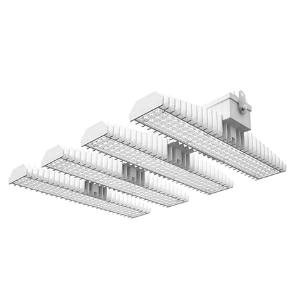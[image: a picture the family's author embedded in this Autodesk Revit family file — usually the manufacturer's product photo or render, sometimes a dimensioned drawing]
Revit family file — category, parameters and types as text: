
# Revit family: 3f_filippi_-_3f_lem_medio_3f_filippi_-_58913_a0811_-_3f_lem_4_led_200_dali_cr_medio___vt_bfc1
name_source: partatom
category: Lighting Fixtures
units: mm (PartAtom-declared; Revit-internal decimal feet)

## family parameters
Cut with Voids When Loaded = No
Host = Face
Light Source = No
Part Type = Normal
Room Calculation Point = No
Round Connector Dimension = Use Diameter
Shared = No

## types (1)
- 3F Filippi - 3F LEM Medio (1 x LED, 30958 lm, 218 W, 4000 K)
    Apparent Load = 218 VA
    Approval mark = CE
    CIE Flux Codes = 83 96 99 100 100
    Color Rendering = 80
    Color Temperature = 4000 K
    Control Gear = Electronic transformer
    Default Elevation = 1800 mm
    Description = Industrial luminaire with high light output and high luminous efficiency designed with the most innovative technologies for environments with temperature up to 55°C.

ILLUMINOTECHNICAL
Luminous efficiency 100% (DLOR 99%, ULOR 1%).
Initial luminous flux of the luminaire 30958 lm.
Medium distribution with rectangular shape.
Installation Interdistance Transv.D = 1.02 x hu - Long.D = 1.06 x hu.
Tabular UGR (CIE 117 - 4H-8H; S=0.25H; 70/50/20): RUG 18.9 - 18.5.
Beam angle: 65° - 67°.
Luminous efficacy 142 lm/W.
Lifetime (L93/B10): 30000 h. (tq+25°C)
Lifetime (L90/B10): 50000 h. (tq+25°C)
Lifetime (L85/B10): 80000 h. (tq+25°C)
Lifetime (L80/B10): 100000 h. (tq+25°C)
Lifetime (L85/B10): 50000 h. (tq+55°C)
Sudden decreased luminous flux after 50000 hours: 0% (C0).
Photobiological safety in compliance with IEC/TR 62778: RG0 risk exempt, (IEC 62471).
In compliance with IEC/EN 62722-2-1 - IEC/EN 62717 standards.

SOURCE
4 Mid-Power linear LED modules 50W/840.
Energy efficiency class (UE 2019/2020 - UE 2019/2015): C.
CIE 13.3 Colour rendering index: CRI >80 (R9 <50%).
IES TM-30 Fidelity Index: Rf = 84 Rg = 95.
CCT nominal colour temperature 4000 K.
Colour initial tolerance (MacAdam): SDCM 3.

MECHANICAL
Passive modular heatsinks in die-casted aluminium, painted in white colour.
To optimize the thermal management of the LED module, the heatsinks are oversized and provided with self-cleaning of cooling fins.
Wiring body in aluminium and galvanised steel anchored solidly to the sinks and thermally separated.
3F Lens lenses with high luminous efficiency, transparent methacrylate (PMMA), fixed to the LED modules.
Fixing brackets in stainless steel.
Luminaire with limited surface temperature. - D - (EN 60598-2-24)
Dimensions: 757x542 mm, height 133 mm. Weight 18.978 kg.
IP65 protection degree.
Mechanical strength to impacts IK06 (1 joule).
Glow-wire test resistance 650°C.

ELECTRICAL
Halogen Free DALI-2 DATI (Parts 251, 252, 253), PUSH-DIM, electronic wiring 230V-50/60Hz, power factor 0.97 at full load, THD <25%, constant output current, class I, 2 driver, 2 DALI addresses.
Power of the luminaire 218 W.
ENEC - CE.
Flicker: <4%.
Luminaire compliant with EN 60598-2-22 for power supply from a centralised emergency system CPSS (Central Power Supply System), not incorporated in the luminaire - high risk areas excluded. The default power and flux are 100% in AC and 15% in DC.
Ambient temperature from -30°C to +55°C.
Temperature class T6 max 85°C.
Quick connection via M25 5P connector with 9-13 mm tightening range.
Power unit positioned on a separate compartment by the LED module to ensure optimum temperatures of cabling components, to be inspectable and maintainable.
Relative humidity UR: <85%.

INSTALLATION
Ceiling / Suspended / Wall.
All accessories dedicated to this product are available on the Catalog and on our website www.3F-Filippi.com.

ACCESSORIES
A0811 - VT transparent glass, tempered, not flammable, with sealing gasket.
One required for each light module. The pack contains 10 pieces.

APPLICATIONS
In commercial environments, exhibition and industrial areas, stores, open areas.
Applications with high ambient temperature up to 55°C.
Environments in which it is necessary a total protection against falling fragments (eg environments with foodstuffs or machines with moving parts or with extreme temperature changes), use luminaires with polycarbonate lenses.

LIGHT MANAGEMENT
Recommended minimum setting: 10%.
The luminaire, equipped with (DALI-2 DATI) driver, can be controlled manually with 3F Easy Dim technology or automatically/manually with wired or wireless DALI/D2D control systems.
The D2D driver guarantees interoperability with other devices with the same certification by making the following information available:
Device Data (Part 251), Energy Report (Part 252), Diagnosis & Maintenance (Part 253).
In electrical systems without a regulation system (manual or automatic) and DALI bus, a suitable jumper must be made on the DA-DA terminals of the appliance.

WARNING
Fixture not suitable for cold stores with an ambient temperature <0°C and/or relative humidity >85%.
Luminaire designed for disposal/recycling at end-of-life.
Replaceable (LED only) light source by a professional. Replaceable control gear by a professional.
    Height = 133 mm  [stored 0.436352 ft]
    Lamp = 1 x LED
    Lamp Light Flux = 30958 lm
    Lamp Power = 218 W
    Lamp count = 1
    Length = 757 mm
    Lifetime = 50000 h
    Luminous efficacy = 142 lm/W
    Manufacturer = 3F Filippi
    ModVariant = No
    Model = 3F Filippi - 58913+A0811 - 3F LEM 4 LED 200 DALI CR MEDIO + VT
    Mounting Place = Ceiling
    Mounting Type = Pendant
    Number of Poles = 1
    OnlyDefault = Yes
    Power Factor = 1
    Product Name = 3F Filippi - 3F LEM Medio
    Product group = pendant luminaire
    ProductGroupID = 9
    Protection Class = Protection class I
    Protection Degree = IP 65
    RLX_Detail_Level = 1
    RLX_Emergency_Light_Flux = 0 lm
    RLX_Emergency_Type = 0
    RLX_Emergency_Type_DB = No
    RlxData = <blob elided: 120201 chars, md5=c76c0ff2>
    Socket = socket
    Standby Power = 0 W
    System Light Flux = 30958 lm
    System Power = 218 W
    Type Comments = Product without accessories
    Type Image = 3f_filippi_-_lem_4__a0811.jpg
    URL = http://relux.com
    VarID = ---
    Voltage = 0 V
    Weight = 0.00 kg
    Width = 542 mm

note: [stored X ft] marks values corroborated as IEEE doubles in the binary element streams (Revit-internal decimal feet)

## geometry (parser evidence)
native form markers: Blend x4, Sweep x13
no freeform markers — native parametric forms only
